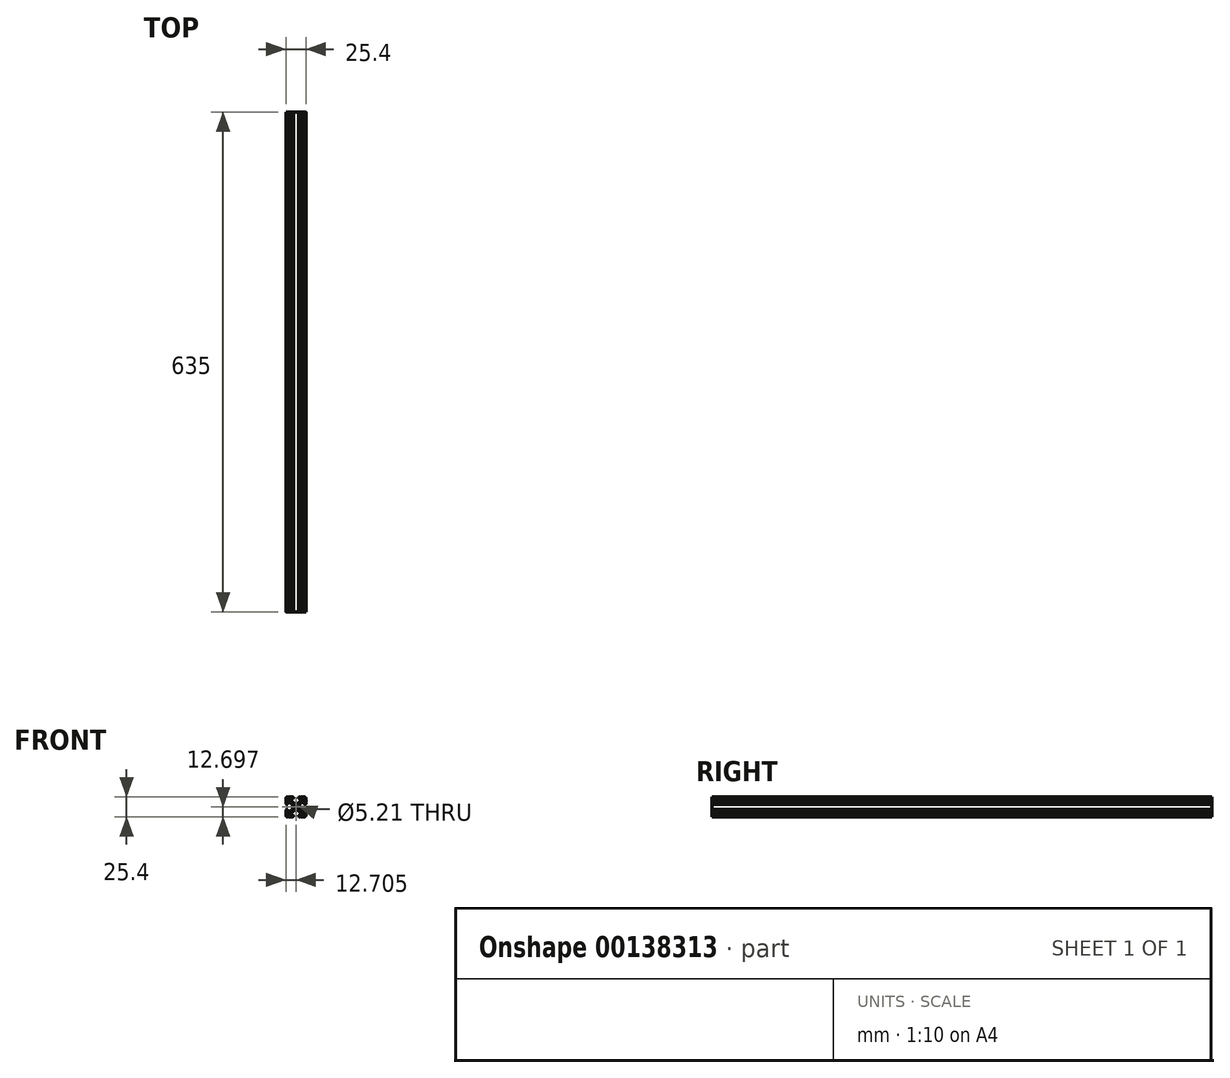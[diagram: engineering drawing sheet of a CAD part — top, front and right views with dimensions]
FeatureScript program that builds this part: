
annotation { "Feature Type Name" : "Feature", "Feature Type Description" : "" }
export const myFeature = defineFeature(function(context is Context, id is Id, definition is map)
    precondition{}
    {
        {
            var Q0;
            Q0=qCreatedBy(makeId("Front.planeOp"),FACE);
            var sketch = newSketch(context, id + "F0", { "sketchPlane" : qUnion([Q0])});
            skLineSegment(sketch, "E0.bottom", {"start": v(-12.7, 12.7) * mm, "end": v(12.7, 12.7) * mm});
            skLineSegment(sketch, "E0.top", {"start": v(-12.7, -12.7) * mm, "end": v(12.7, -12.7) * mm});
            skLineSegment(sketch, "E0.left", {"start": v(-12.7, 12.7) * mm, "end": v(-12.7, -12.7) * mm});
            skLineSegment(sketch, "E0.right", {"start": v(12.7, 12.7) * mm, "end": v(12.7, -12.7) * mm});
            skPoint(sketch, "E0.middle", {"position": v(0, 0) * mm});
            skLineSegment(sketch, "E1.bottom", {"start": v(-0.33, 4.52) * mm, "end": v(0.33, 4.52) * mm});
            skLineSegment(sketch, "E1.right", {"start": v(4.52, 3.37) * mm, "end": v(4.52, -2.64) * mm});
            skCircle(sketch, "E2", {"center": v(0, 0) * mm, "radius": 2.6 * mm});
            skLineSegment(sketch, "E3.0", {"start": v(-0.87, 4.74) * mm, "end": v(-7.97, 11.84) * mm});
            skLineSegment(sketch, "E4.0", {"start": v(-5.3, 3.74) * mm, "end": v(-13.48, 11.92) * mm});
            skLineSegment(sketch, "E5.MirrorCS", {"start": v(0.87, 4.74) * mm, "end": v(7.97, 11.84) * mm});
            skLineSegment(sketch, "E6.MirrorCS", {"start": v(5.3, 3.74) * mm, "end": v(13.48, 11.92) * mm});
            skLineSegment(sketch, "E7.MirrorCS", {"start": v(-4.64, 3.08) * mm, "end": v(-13.48, 11.92) * mm});
            skLineSegment(sketch, "E8.MirrorCS", {"start": v(-4.74, -3.18) * mm, "end": v(-13.48, -11.92) * mm});
            skLineSegment(sketch, "E9.MirrorCS", {"start": v(-5.3, -3.74) * mm, "end": v(-13.48, -11.92) * mm});
            skLineSegment(sketch, "E10.MirrorCS", {"start": v(-0.87, -4.74) * mm, "end": v(-7.97, -11.84) * mm});
            skLineSegment(sketch, "E11.MirrorCS", {"start": v(0.64, -4.52) * mm, "end": v(7.97, -11.84) * mm});
            skLineSegment(sketch, "E12.MirrorCS", {"start": v(0.87, -4.74) * mm, "end": v(7.97, -11.84) * mm});
            skLineSegment(sketch, "E13.MirrorCS", {"start": v(4.74, -3.18) * mm, "end": v(13.48, -11.92) * mm});
            skPoint(sketch, "E14.orphan", {"position": v(-5.3, 3.74) * mm});
            skPoint(sketch, "E15.orphan", {"position": v(-5.3, -3.74) * mm});
            skArc(sketch, "E16.filletArc", {"start": v(-0.33, -4.52) * mm, "mid": v(-0.62, -4.58) * mm, "end": v(-0.87, -4.74) * mm});
            skArc(sketch, "E17.filletArc", {"start": v(-4.74, -3.18) * mm, "mid": v(-4.58, -2.93) * mm, "end": v(-4.52, -2.64) * mm});
            skLineSegment(sketch, "E18", {"start": v(-4.52, -2.64) * mm, "end": v(-4.52, 2.41) * mm});
            skArc(sketch, "E19.filletArc", {"start": v(-0.87, 4.74) * mm, "mid": v(-0.62, 4.58) * mm, "end": v(-0.33, 4.52) * mm});
            skArc(sketch, "E20.filletArc", {"start": v(0.33, 4.52) * mm, "mid": v(0.62, 4.58) * mm, "end": v(0.87, 4.74) * mm});
            skArc(sketch, "E21.filletArc", {"start": v(4.52, -2.64) * mm, "mid": v(4.58, -2.93) * mm, "end": v(4.74, -3.18) * mm});
            skLineSegment(sketch, "E22", {"start": v(-0.33, -4.52) * mm, "end": v(0.33, -4.52) * mm});
            skPoint(sketch, "E23.visualSharp", {"position": v(0.64, -4.52) * mm});
            skArc(sketch, "E23.filletArc", {"start": v(0.87, -4.74) * mm, "mid": v(0.62, -4.58) * mm, "end": v(0.33, -4.52) * mm});
            skArc(sketch, "E24", {"start": v(-120.05, 65.1) * mm, "mid": v(-119.54, 65.6) * mm, "end": v(-120.05, 66.12) * mm});
            skLineSegment(sketch, "E25", {"start": v(-120.05, 69.33) * mm, "end": v(-120.05, 66.12) * mm});
            skArc(sketch, "E26", {"start": v(-120.05, 69.33) * mm, "mid": v(-119.54, 69.84) * mm, "end": v(-120.05, 70.35) * mm});
            skLineSegment(sketch, "E27", {"start": v(-120.05, 71.32) * mm, "end": v(-120.05, 70.35) * mm});
            skArc(sketch, "E28", {"start": v(-117.84, 71.32) * mm, "mid": v(-118.94, 72.43) * mm, "end": v(-120.05, 71.32) * mm});
            skLineSegment(sketch, "E29", {"start": v(-117.84, 69.2) * mm, "end": v(-117.84, 71.32) * mm});
            skArc(sketch, "E30", {"start": v(-117.84, 69.2) * mm, "mid": v(-117.2, 68.25) * mm, "end": v(-116.1, 68.47) * mm});
            skLineSegment(sketch, "E31", {"start": v(-112.77, 71.8) * mm, "end": v(-116.1, 68.47) * mm});
            skArc(sketch, "E32", {"start": v(-112.77, 71.8) * mm, "mid": v(-112.08, 72.83) * mm, "end": v(-111.84, 74.05) * mm});
            skLineSegment(sketch, "E33", {"start": v(-111.84, 77.28) * mm, "end": v(-111.84, 74.05) * mm});
            skArc(sketch, "E34", {"start": v(-111.84, 77.28) * mm, "mid": v(-112.08, 78.5) * mm, "end": v(-112.77, 79.53) * mm});
            skLineSegment(sketch, "E35", {"start": v(-116.1, 82.86) * mm, "end": v(-112.77, 79.53) * mm});
            skArc(sketch, "E36", {"start": v(-116.1, 82.86) * mm, "mid": v(-117.2, 83.08) * mm, "end": v(-117.84, 82.14) * mm});
            skLineSegment(sketch, "E37", {"start": v(-117.84, 80.01) * mm, "end": v(-117.84, 82.14) * mm});
            skArc(sketch, "E38", {"start": v(-120.05, 80.01) * mm, "mid": v(-118.94, 78.9) * mm, "end": v(-117.84, 80.01) * mm});
            skLineSegment(sketch, "E39", {"start": v(-120.05, 80.98) * mm, "end": v(-120.05, 80.01) * mm});
            skArc(sketch, "E40", {"start": v(-120.05, 80.98) * mm, "mid": v(-119.54, 81.5) * mm, "end": v(-120.05, 82) * mm});
            skLineSegment(sketch, "E41", {"start": v(-120.05, 85.22) * mm, "end": v(-120.05, 82) * mm});
            skArc(sketch, "E42", {"start": v(-120.05, 85.22) * mm, "mid": v(-119.54, 85.72) * mm, "end": v(-120.05, 86.23) * mm});
            skArc(sketch, "E43", {"start": v(-117.91, 88.37) * mm, "mid": v(-119.43, 87.75) * mm, "end": v(-120.05, 86.23) * mm});
            skArc(sketch, "E44", {"start": v(-117.91, 88.37) * mm, "mid": v(-117.4, 87.86) * mm, "end": v(-116.9, 88.37) * mm});
            skLineSegment(sketch, "E45", {"start": v(-113.68, 88.37) * mm, "end": v(-116.9, 88.37) * mm});
            skArc(sketch, "E46", {"start": v(-113.68, 88.37) * mm, "mid": v(-113.17, 87.86) * mm, "end": v(-112.66, 88.37) * mm});
            skLineSegment(sketch, "E47", {"start": v(-111.69, 88.37) * mm, "end": v(-112.66, 88.37) * mm});
            skArc(sketch, "E48", {"start": v(-111.69, 86.16) * mm, "mid": v(-110.58, 87.26) * mm, "end": v(-111.69, 88.37) * mm});
            skLineSegment(sketch, "E49", {"start": v(-113.82, 86.16) * mm, "end": v(-111.69, 86.16) * mm});
            skArc(sketch, "E50", {"start": v(-113.82, 86.16) * mm, "mid": v(-114.76, 85.53) * mm, "end": v(-114.54, 84.42) * mm});
            skLineSegment(sketch, "E51", {"start": v(-111.2, 81.1) * mm, "end": v(-114.54, 84.42) * mm});
            skArc(sketch, "E52", {"start": v(-111.2, 81.1) * mm, "mid": v(-110.18, 80.4) * mm, "end": v(-108.96, 80.16) * mm});
            skLineSegment(sketch, "E53", {"start": v(-105.73, 80.16) * mm, "end": v(-108.96, 80.16) * mm});
            skArc(sketch, "E54", {"start": v(-105.73, 80.16) * mm, "mid": v(-104.51, 80.4) * mm, "end": v(-103.48, 81.1) * mm});
            skLineSegment(sketch, "E55", {"start": v(-100.15, 84.42) * mm, "end": v(-103.48, 81.1) * mm});
            skArc(sketch, "E56", {"start": v(-100.15, 84.42) * mm, "mid": v(-99.93, 85.53) * mm, "end": v(-100.87, 86.16) * mm});
            skLineSegment(sketch, "E57", {"start": v(-103, 86.16) * mm, "end": v(-100.87, 86.16) * mm});
            skArc(sketch, "E58", {"start": v(-103, 88.37) * mm, "mid": v(-104.1, 87.26) * mm, "end": v(-103, 86.16) * mm});
            skLineSegment(sketch, "E59", {"start": v(-102.03, 88.37) * mm, "end": v(-103, 88.37) * mm});
            skArc(sketch, "E60", {"start": v(-102.03, 88.37) * mm, "mid": v(-101.52, 87.86) * mm, "end": v(-101.01, 88.37) * mm});
            skLineSegment(sketch, "E61", {"start": v(-97.8, 88.37) * mm, "end": v(-101.01, 88.37) * mm});
            skArc(sketch, "E62", {"start": v(-97.8, 88.37) * mm, "mid": v(-97.29, 87.86) * mm, "end": v(-96.78, 88.37) * mm});
            skArc(sketch, "E63", {"start": v(-94.65, 86.23) * mm, "mid": v(-95.26, 87.75) * mm, "end": v(-96.78, 88.37) * mm});
            skArc(sketch, "E64", {"start": v(-94.65, 86.23) * mm, "mid": v(-95.15, 85.72) * mm, "end": v(-94.65, 85.22) * mm});
            skLineSegment(sketch, "E65", {"start": v(-94.65, 82) * mm, "end": v(-94.65, 85.22) * mm});
            skArc(sketch, "E66", {"start": v(-94.65, 82) * mm, "mid": v(-95.15, 81.5) * mm, "end": v(-94.65, 80.98) * mm});
            skLineSegment(sketch, "E67", {"start": v(-94.65, 80.01) * mm, "end": v(-94.65, 80.98) * mm});
            skArc(sketch, "E68", {"start": v(-96.86, 80.01) * mm, "mid": v(-95.75, 78.9) * mm, "end": v(-94.65, 80.01) * mm});
            skLineSegment(sketch, "E69", {"start": v(-96.86, 82.14) * mm, "end": v(-96.86, 80.01) * mm});
            skArc(sketch, "E70", {"start": v(-96.86, 82.14) * mm, "mid": v(-97.48, 83.08) * mm, "end": v(-98.59, 82.86) * mm});
            skLineSegment(sketch, "E71", {"start": v(-101.92, 79.53) * mm, "end": v(-98.59, 82.86) * mm});
            skArc(sketch, "E72", {"start": v(-101.92, 79.53) * mm, "mid": v(-102.6, 78.5) * mm, "end": v(-102.85, 77.28) * mm});
            skLineSegment(sketch, "E73", {"start": v(-102.85, 74.05) * mm, "end": v(-102.85, 77.28) * mm});
            skArc(sketch, "E74", {"start": v(-102.85, 74.05) * mm, "mid": v(-102.6, 72.83) * mm, "end": v(-101.92, 71.8) * mm});
            skLineSegment(sketch, "E75", {"start": v(-98.59, 68.47) * mm, "end": v(-101.92, 71.8) * mm});
            skArc(sketch, "E76", {"start": v(-98.59, 68.47) * mm, "mid": v(-97.48, 68.25) * mm, "end": v(-96.86, 69.2) * mm});
            skLineSegment(sketch, "E77", {"start": v(-96.86, 71.32) * mm, "end": v(-96.86, 69.2) * mm});
            skArc(sketch, "E78", {"start": v(-94.65, 71.32) * mm, "mid": v(-95.75, 72.43) * mm, "end": v(-96.86, 71.32) * mm});
            skLineSegment(sketch, "E79", {"start": v(-94.65, 70.35) * mm, "end": v(-94.65, 71.32) * mm});
            skArc(sketch, "E80", {"start": v(-94.65, 70.35) * mm, "mid": v(-95.15, 69.84) * mm, "end": v(-94.65, 69.33) * mm});
            skLineSegment(sketch, "E81", {"start": v(-94.65, 66.12) * mm, "end": v(-94.65, 69.33) * mm});
            skArc(sketch, "E82", {"start": v(-94.65, 66.12) * mm, "mid": v(-95.15, 65.6) * mm, "end": v(-94.65, 65.1) * mm});
            skArc(sketch, "E83", {"start": v(-96.78, 62.97) * mm, "mid": v(-95.26, 63.58) * mm, "end": v(-94.65, 65.1) * mm});
            skArc(sketch, "E84", {"start": v(-96.78, 62.97) * mm, "mid": v(-97.29, 63.47) * mm, "end": v(-97.8, 62.97) * mm});
            skLineSegment(sketch, "E85", {"start": v(-101.01, 62.97) * mm, "end": v(-97.8, 62.97) * mm});
            skArc(sketch, "E86", {"start": v(-101.01, 62.97) * mm, "mid": v(-101.52, 63.47) * mm, "end": v(-102.03, 62.97) * mm});
            skLineSegment(sketch, "E87", {"start": v(-103, 62.97) * mm, "end": v(-102.03, 62.97) * mm});
            skArc(sketch, "E88", {"start": v(-103, 65.18) * mm, "mid": v(-104.1, 64.07) * mm, "end": v(-103, 62.97) * mm});
            skLineSegment(sketch, "E89", {"start": v(-100.87, 65.18) * mm, "end": v(-103, 65.18) * mm});
            skArc(sketch, "E90", {"start": v(-100.87, 65.18) * mm, "mid": v(-99.93, 65.8) * mm, "end": v(-100.15, 66.91) * mm});
            skLineSegment(sketch, "E91", {"start": v(-103.48, 70.24) * mm, "end": v(-100.15, 66.91) * mm});
            skArc(sketch, "E92", {"start": v(-103.48, 70.24) * mm, "mid": v(-104.51, 70.93) * mm, "end": v(-105.73, 71.17) * mm});
            skLineSegment(sketch, "E93", {"start": v(-108.96, 71.17) * mm, "end": v(-105.73, 71.17) * mm});
            skArc(sketch, "E94", {"start": v(-108.96, 71.17) * mm, "mid": v(-110.18, 70.93) * mm, "end": v(-111.2, 70.24) * mm});
            skLineSegment(sketch, "E95", {"start": v(-114.54, 66.91) * mm, "end": v(-111.2, 70.24) * mm});
            skArc(sketch, "E96", {"start": v(-114.54, 66.91) * mm, "mid": v(-114.76, 65.8) * mm, "end": v(-113.82, 65.18) * mm});
            skLineSegment(sketch, "E97", {"start": v(-111.69, 65.18) * mm, "end": v(-113.82, 65.18) * mm});
            skArc(sketch, "E98", {"start": v(-111.69, 62.97) * mm, "mid": v(-110.58, 64.07) * mm, "end": v(-111.69, 65.18) * mm});
            skLineSegment(sketch, "E99", {"start": v(-112.66, 62.97) * mm, "end": v(-111.69, 62.97) * mm});
            skArc(sketch, "E100", {"start": v(-112.66, 62.97) * mm, "mid": v(-113.17, 63.47) * mm, "end": v(-113.68, 62.97) * mm});
            skLineSegment(sketch, "E101", {"start": v(-116.9, 62.97) * mm, "end": v(-113.68, 62.97) * mm});
            skArc(sketch, "E102", {"start": v(-116.9, 62.97) * mm, "mid": v(-117.4, 63.47) * mm, "end": v(-117.91, 62.97) * mm});
            skArc(sketch, "E103", {"start": v(-120.05, 65.1) * mm, "mid": v(-119.43, 63.58) * mm, "end": v(-117.91, 62.97) * mm});
            skCircle(sketch, "E104", {"center": v(-107.35, 75.67) * mm, "radius": 2.6 * mm});
            skSolve(sketch);
        }
        {
            var Q0;
            Q0=makeQuery(id+"F0.imprint","IMPRINT",FACE,{"disambiguationData":[TD([[makeQuery(id+"F0.imprint","IMPRINT",EDGE,{"derivedFrom":sQuery(id+"F0.wireOp",EDGE,"E24")}),-1.0]])]});
            extrude(context, id + "F1", {"entities" : qUnion([Q0]), "endBound" : BoundingType.SYMMETRIC, "depth" : 635 * mm});
        }
    });
